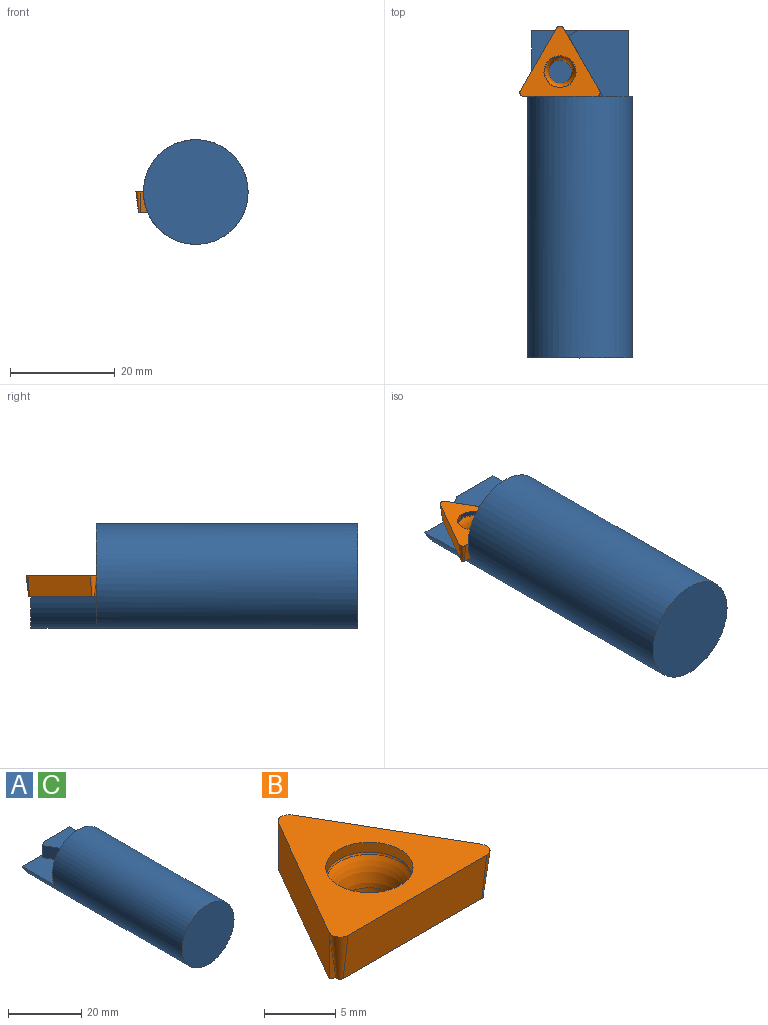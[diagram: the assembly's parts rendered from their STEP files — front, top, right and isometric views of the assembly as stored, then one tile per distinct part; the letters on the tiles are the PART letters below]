
ASSEMBLY  parts=3 mates=1
PART A: 13 faces, bbox 20x62.5x20 mm
  f0: plane 20x20mm, normal (0,1,0), area 215.9mm2, adj f1,f2,f5,f6,f7,f8,f12
  f1: plane 12.54x9.85mm, normal (0,0,-1), area 2.1mm2, adj f0,f4,f8,f9,f10,f11,f12
  f2: cylinder r=10mm len=50mm, axis (0,1,0), area 3141.6mm2, adj f0,f3,f10
  f3: plane 20x20mm, normal (0,-1,0), area 314.2mm2, adj f2
  f4: plane 4x1.73mm, normal (-0.5,0.87,0), area 8mm2, adj f1,f5,f6,f7,f11
  f5: plane 11.54x6.66mm, normal (-0.87,-0.5,0), area 53.3mm2, adj f0,f4,f6,f7
  f6: plane 12.54x11.51mm, normal (0,0,1), area 105mm2, adj f0,f4,f5,f11,f12
  f7: plane 13.58x12.5mm, normal (0,0,1), area 125.7mm2, adj f0,f4,f5,f8,f9
  f8: cylinder r=9.98mm len=18.3mm, axis (0,-1,0), area 289.2mm2, adj f0,f1,f7,f9
  f9: plane 18.3x5.98mm, normal (0,1,0), area 78.9mm2, adj f1,f7,f8
  f10: plane 0.28x0.12mm, normal (0,-1,0), area 0mm2, adj f1,f2,f12
  f11: plane 9.78x4mm, normal (0,1,0), area 39.1mm2, adj f1,f4,f6,f12
  f12: plane 12.54x4mm, normal (1,0,0), area 50.2mm2, adj f0,f1,f6,f10,f11
PART B: 16 faces, bbox 15.3x13.5x6.1 mm
  f0: plane 14.36x12.52mm, normal (0,0,-1), area 75.4mm2, adj f1,f2,f4,f5,f6,f9,f11,f12
  f1: plane 13.75x3.97mm, normal (0,-0.99,-0.12), area 55mm2, adj f0,f3,f4,f5
  f2: plane 12.15x7.3mm, normal (0.86,0.5,-0.12), area 55mm2, adj f0,f3,f4,f6
  f3: plane 15.34x13.49mm, normal (0,0,1), area 87.1mm2, adj f1,f2,f4,f5,f6,f7,f14
  f4: cone r=0.79mm half-angle=7deg, axis (0,0,1), area 4.6mm2, adj f0,f1,f2,f3
  f5: cone r=0.79mm half-angle=7deg, axis (0,0,1), area 4.6mm2, adj f0,f1,f3,f12
  f6: cone r=0.79mm half-angle=7deg, axis (0,0,1), area 4.6mm2, adj f0,f2,f3,f13
  f7: cone r=3mm half-angle=4deg, axis (0,0,1), area 15.5mm2, adj f3,f10
  f8: torus R=6.2mm, axis (0,0,1), area 38.4mm2, adj f9,f10
  f9: cylinder r=2.2mm len=4.4mm, axis (0,0,1), area 9.2mm2, adj f0,f8
  f10: torus R=2.71mm, axis (0,0,-1), area 3.1mm2, adj f7,f8
  f11: plane 11.91x6.87mm, normal (0.87,-0.5,0), area 0.4mm2, adj f0,f12,f13,f15
  f12: plane 4x0.69mm, normal (-0.5,-0.87,0), area 1mm2, adj f0,f5,f11,f14,f15
  f13: plane 4x0.69mm, normal (0.5,0.87,0), area 1mm2, adj f0,f6,f11,f14,f15
  f14: plane 11.91x6.87mm, normal (-0.87,0.5,0), area 55mm2, adj f3,f12,f13,f15
  f15: plane 12.3x7.56mm, normal (0,0,-1), area 10.9mm2, adj f11,f12,f13,f14
PART C: same geometry as A
PLACE A t=(11.06,2.84,-28.08)mm
PLACE B rot(axis=(0,0,-1),120deg) t=(7.28,17.06,-28.08)mm
PLACE C t=(11.06,2.84,-28.08)mm
MATE planar B.f14 <-> C.f5  axis (0.87,0.5,0) through (11.41,9.91,-30.08)mm
